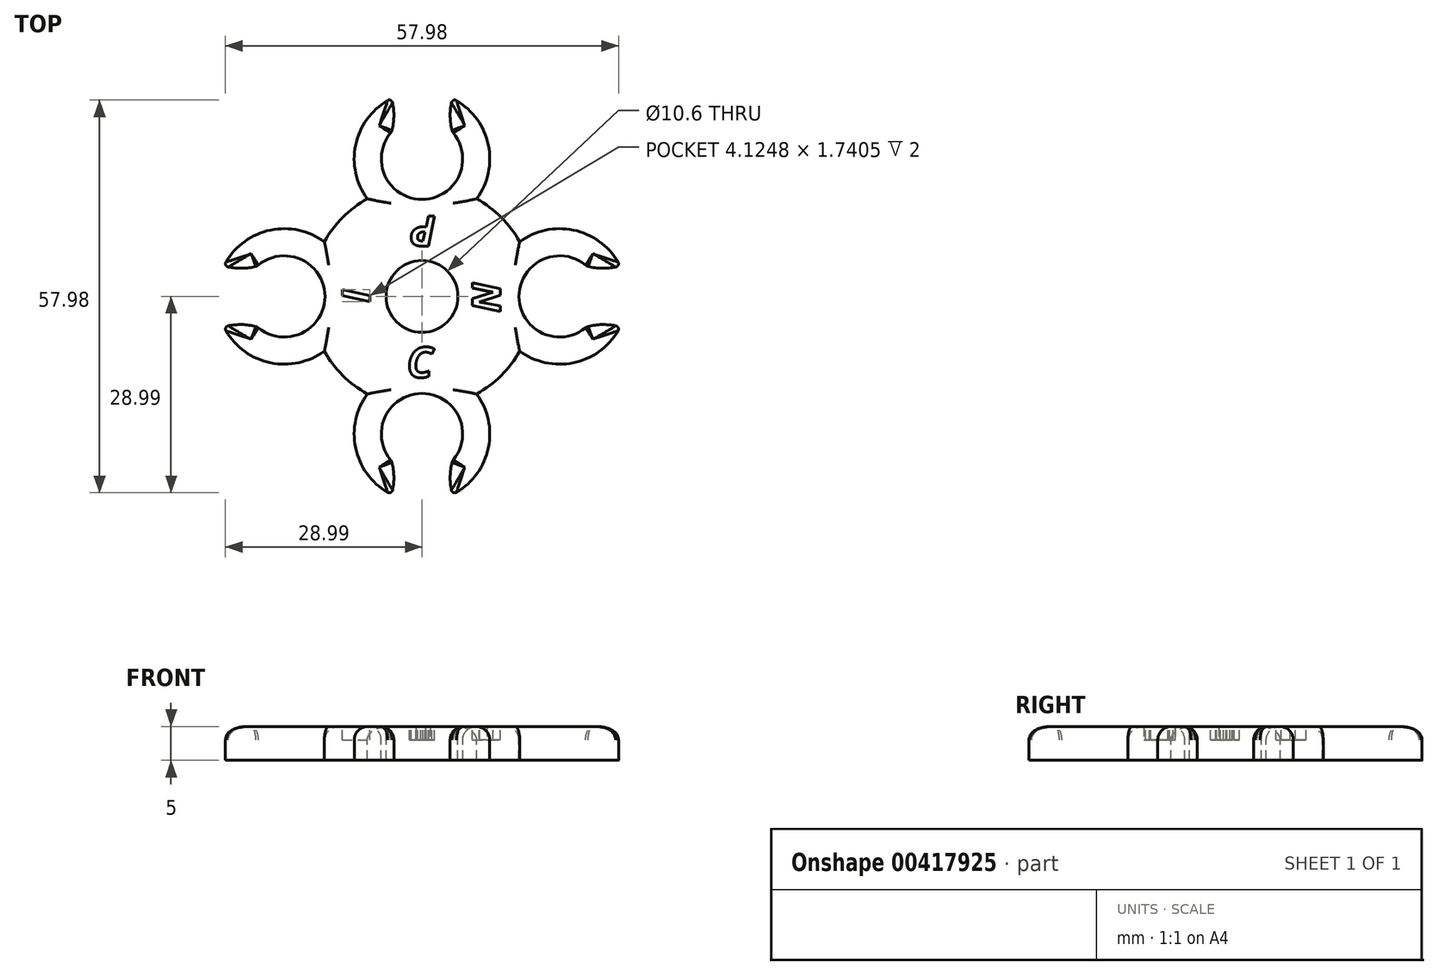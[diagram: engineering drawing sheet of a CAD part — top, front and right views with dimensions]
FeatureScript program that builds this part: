
annotation { "Feature Type Name" : "Feature", "Feature Type Description" : "" }
export const myFeature = defineFeature(function(context is Context, id is Id, definition is map)
    precondition{}
    {
        {
            var Q0;
            Q0=qCreatedBy(makeId("Top.planeOp"),FACE);
            var sketch = newSketch(context, id + "F0", { "sketchPlane" : qUnion([Q0])});
            skArc(sketch, "E0", {"start": v(24.12, 4.63) * mm, "mid": v(14.31, 0) * mm, "end": v(24.12, -4.63) * mm});
            skArc(sketch, "E1", {"start": v(28.92, 5.08) * mm, "mid": v(22.33, 9.8) * mm, "end": v(14.41, 8.07) * mm});
            skArc(sketch, "E2", {"start": v(24.5, 4.44) * mm, "mid": v(26.55, 4.15) * mm, "end": v(28.6, 4.34) * mm});
            skArc(sketch, "E3", {"start": v(28.6, -4.34) * mm, "mid": v(26.55, -4.15) * mm, "end": v(24.5, -4.44) * mm});
            skArc(sketch, "E4.filletArc", {"start": v(28.6, 4.34) * mm, "mid": v(28.95, 4.63) * mm, "end": v(28.92, 5.08) * mm});
            skArc(sketch, "E5.filletArc", {"start": v(28.92, -5.08) * mm, "mid": v(28.95, -4.63) * mm, "end": v(28.6, -4.34) * mm});
            skArc(sketch, "E6.filletArc", {"start": v(24.5, -4.44) * mm, "mid": v(24.3, -4.51) * mm, "end": v(24.12, -4.63) * mm});
            skArc(sketch, "E7.filletArc", {"start": v(24.12, 4.63) * mm, "mid": v(24.3, 4.51) * mm, "end": v(24.5, 4.44) * mm});
            skCircle(sketch, "E8", {"center": v(0, 0) * mm, "radius": 5.3 * mm});
            skArc(sketch, "E9.1.0", {"start": v(-4.63, 24.12) * mm, "mid": v(0, 14.31) * mm, "end": v(4.63, 24.12) * mm});
            skArc(sketch, "E9.1.1", {"start": v(-5.08, 28.92) * mm, "mid": v(-9.8, 22.33) * mm, "end": v(-8.07, 14.41) * mm});
            skArc(sketch, "E9.1.2", {"start": v(-4.44, 24.5) * mm, "mid": v(-4.15, 26.55) * mm, "end": v(-4.34, 28.6) * mm});
            skArc(sketch, "E9.1.3", {"start": v(4.34, 28.6) * mm, "mid": v(4.15, 26.55) * mm, "end": v(4.44, 24.5) * mm});
            skArc(sketch, "E9.1.4", {"start": v(4.44, 24.5) * mm, "mid": v(4.51, 24.3) * mm, "end": v(4.63, 24.12) * mm});
            skArc(sketch, "E9.1.5", {"start": v(-4.63, 24.12) * mm, "mid": v(-4.51, 24.3) * mm, "end": v(-4.44, 24.5) * mm});
            skArc(sketch, "E9.1.6", {"start": v(-4.34, 28.6) * mm, "mid": v(-4.63, 28.95) * mm, "end": v(-5.08, 28.92) * mm});
            skArc(sketch, "E9.1.7", {"start": v(5.08, 28.92) * mm, "mid": v(4.63, 28.95) * mm, "end": v(4.34, 28.6) * mm});
            skArc(sketch, "E9.2.0", {"start": v(-24.12, -4.63) * mm, "mid": v(-14.31, 0) * mm, "end": v(-24.12, 4.63) * mm});
            skArc(sketch, "E9.2.1", {"start": v(-28.92, -5.08) * mm, "mid": v(-22.33, -9.8) * mm, "end": v(-14.41, -8.07) * mm});
            skArc(sketch, "E9.2.2", {"start": v(-24.5, -4.44) * mm, "mid": v(-26.55, -4.15) * mm, "end": v(-28.6, -4.34) * mm});
            skArc(sketch, "E9.2.3", {"start": v(-28.6, 4.34) * mm, "mid": v(-26.55, 4.15) * mm, "end": v(-24.5, 4.44) * mm});
            skArc(sketch, "E9.2.4", {"start": v(-24.5, 4.44) * mm, "mid": v(-24.3, 4.51) * mm, "end": v(-24.12, 4.63) * mm});
            skArc(sketch, "E9.2.5", {"start": v(-24.12, -4.63) * mm, "mid": v(-24.3, -4.51) * mm, "end": v(-24.5, -4.44) * mm});
            skArc(sketch, "E9.2.6", {"start": v(-28.6, -4.34) * mm, "mid": v(-28.95, -4.63) * mm, "end": v(-28.92, -5.08) * mm});
            skArc(sketch, "E9.2.7", {"start": v(-28.92, 5.08) * mm, "mid": v(-28.95, 4.63) * mm, "end": v(-28.6, 4.34) * mm});
            skArc(sketch, "E9.3.0", {"start": v(4.63, -24.12) * mm, "mid": v(0, -14.31) * mm, "end": v(-4.63, -24.12) * mm});
            skArc(sketch, "E9.3.1", {"start": v(5.08, -28.92) * mm, "mid": v(9.8, -22.33) * mm, "end": v(8.07, -14.41) * mm});
            skArc(sketch, "E9.3.2", {"start": v(4.44, -24.5) * mm, "mid": v(4.15, -26.55) * mm, "end": v(4.34, -28.6) * mm});
            skArc(sketch, "E9.3.3", {"start": v(-4.34, -28.6) * mm, "mid": v(-4.15, -26.55) * mm, "end": v(-4.44, -24.5) * mm});
            skArc(sketch, "E9.3.4", {"start": v(-4.44, -24.5) * mm, "mid": v(-4.51, -24.3) * mm, "end": v(-4.63, -24.12) * mm});
            skArc(sketch, "E9.3.5", {"start": v(4.63, -24.12) * mm, "mid": v(4.51, -24.3) * mm, "end": v(4.44, -24.5) * mm});
            skArc(sketch, "E9.3.6", {"start": v(4.34, -28.6) * mm, "mid": v(4.63, -28.95) * mm, "end": v(5.08, -28.92) * mm});
            skArc(sketch, "E9.3.7", {"start": v(-5.08, -28.92) * mm, "mid": v(-4.63, -28.95) * mm, "end": v(-4.34, -28.6) * mm});
            skArc(sketch, "E10", {"start": v(-8.07, 14.41) * mm, "mid": v(-11.68, 11.68) * mm, "end": v(-14.41, 8.07) * mm});
            skArc(sketch, "E11.trimOffspring", {"start": v(14.41, 8.07) * mm, "mid": v(11.68, 11.68) * mm, "end": v(8.07, 14.41) * mm});
            skArc(sketch, "E12.trimOffspring", {"start": v(8.07, -14.41) * mm, "mid": v(11.68, -11.68) * mm, "end": v(14.41, -8.07) * mm});
            skArc(sketch, "E13.trimOffspring", {"start": v(-14.41, -8.07) * mm, "mid": v(-11.68, -11.68) * mm, "end": v(-8.07, -14.41) * mm});
            skLineSegment(sketch, "E14.bottom", {"start": v(-2.08, -7.47) * mm, "end": v(2.08, -7.47) * mm, "construction": true});
            skLineSegment(sketch, "E14.top", {"start": v(-2.08, -11.97) * mm, "end": v(2.08, -11.97) * mm, "construction": true});
            skLineSegment(sketch, "E14.left", {"start": v(-2.08, -7.47) * mm, "end": v(-2.08, -11.97) * mm, "construction": true});
            skLineSegment(sketch, "E14.right", {"start": v(2.08, -7.47) * mm, "end": v(2.08, -11.97) * mm, "construction": true});
            skPoint(sketch, "E14.middle", {"position": v(0, -9.72) * mm});
            skLineSegment(sketch, "E15.1.0", {"start": v(7.39, -2.08) * mm, "end": v(7.39, 2.08) * mm, "construction": true});
            skLineSegment(sketch, "E15.1.1", {"start": v(7.39, -2.08) * mm, "end": v(11.89, -2.08) * mm, "construction": true});
            skLineSegment(sketch, "E15.1.2", {"start": v(11.89, -2.08) * mm, "end": v(11.89, 2.08) * mm, "construction": true});
            skLineSegment(sketch, "E15.1.3", {"start": v(7.39, 2.08) * mm, "end": v(11.89, 2.08) * mm, "construction": true});
            skLineSegment(sketch, "E15.2.0", {"start": v(2, 7.39) * mm, "end": v(-2.16, 7.39) * mm, "construction": true});
            skLineSegment(sketch, "E15.2.1", {"start": v(2, 7.39) * mm, "end": v(2, 11.89) * mm, "construction": true});
            skLineSegment(sketch, "E15.2.2", {"start": v(2, 11.89) * mm, "end": v(-2.16, 11.89) * mm, "construction": true});
            skLineSegment(sketch, "E15.2.3", {"start": v(-2.16, 7.39) * mm, "end": v(-2.16, 11.89) * mm, "construction": true});
            skLineSegment(sketch, "E15.3.0", {"start": v(-7.47, 2) * mm, "end": v(-7.47, -2.16) * mm, "construction": true});
            skLineSegment(sketch, "E15.3.1", {"start": v(-7.47, 2) * mm, "end": v(-11.97, 2) * mm, "construction": true});
            skLineSegment(sketch, "E15.3.2", {"start": v(-11.97, 2) * mm, "end": v(-11.97, -2.16) * mm, "construction": true});
            skLineSegment(sketch, "E15.3.3", {"start": v(-7.47, -2.16) * mm, "end": v(-11.97, -2.16) * mm, "construction": true});
            skPoint(sketch, "E15.center", {"position": v(-0.04, -0.04) * mm});
            skText(sketch, "E16", { "text": "C", "fontName": "OpenSans-BoldItalic.ttf"});
            skText(sketch, "E17", { "text": "N", "fontName": "OpenSans-BoldItalic.ttf"});
            skText(sketch, "E18", { "text": "P", "fontName": "OpenSans-BoldItalic.ttf"});
            skText(sketch, "E19", { "text": "I", "fontName": "OpenSans-BoldItalic.ttf"});
            skArc(sketch, "E20.trimOffspring", {"start": v(-14.41, 8.07) * mm, "mid": v(-22.33, 9.8) * mm, "end": v(-28.92, 5.08) * mm});
            skArc(sketch, "E21.trimOffspring", {"start": v(-8.07, -14.41) * mm, "mid": v(-9.8, -22.33) * mm, "end": v(-5.08, -28.92) * mm});
            skArc(sketch, "E22.trimOffspring", {"start": v(14.41, -8.07) * mm, "mid": v(22.33, -9.8) * mm, "end": v(28.92, -5.08) * mm});
            skArc(sketch, "E23.trimOffspring", {"start": v(8.07, 14.41) * mm, "mid": v(9.8, 22.33) * mm, "end": v(5.08, 28.92) * mm});
            const initialGuessF0  = {"E16": [-0.00223, -0.01197, 1, 0, 0.0045], "E17": [0.01155, -0.00236, 0, 1, 0.00416], "E18": [0.00203, 0.01189, -1, 0, 0.0045], "E19": [-0.01178, 0.00113, 0, -1, 0.00416]};
            skSetInitialGuess(sketch, initialGuessF0);
            skSolve(sketch);
        }
        {
            var Q0;
            Q0=makeQuery(id+"F0.imprint","IMPRINT",FACE,{"disambiguationData":[TD([[makeQuery(id+"F0.imprint","IMPRINT",EDGE,{"derivedFrom":sQuery(id+"F0.wireOp",EDGE,"E19.sketch_text.stroke-0")}),-1.0]])]});
            var Q1;
            Q1=makeQuery(id+"F0.imprint","IMPRINT",FACE,{"disambiguationData":[TD([[makeQuery(id+"F0.imprint","IMPRINT",EDGE,{"derivedFrom":sQuery(id+"F0.wireOp",EDGE,"E8")}),-1.0]])]});
            var Q2;
            Q2=makeQuery(id+"F0.imprint","IMPRINT",FACE,{"disambiguationData":[TD([[makeQuery(id+"F0.imprint","IMPRINT",EDGE,{"derivedFrom":sQuery(id+"F0.wireOp",EDGE,"E18.sketch_text.stroke-0")}),-1.0]])]});
            var Q3;
            Q3=makeQuery(id+"F0.imprint","IMPRINT",FACE,{"disambiguationData":[TD([[makeQuery(id+"F0.imprint","IMPRINT",EDGE,{"derivedFrom":sQuery(id+"F0.wireOp",EDGE,"E18.sketch_text.stroke-0")}),1.0]])]});
            var Q4;
            Q4=makeQuery(id+"F0.imprint","IMPRINT",FACE,{"disambiguationData":[TD([[makeQuery(id+"F0.imprint","IMPRINT",EDGE,{"derivedFrom":sQuery(id+"F0.wireOp",EDGE,"E17.sketch_text.stroke-0")}),-1.0]])]});
            var Q5;
            Q5=makeQuery(id+"F0.imprint","IMPRINT",FACE,{"disambiguationData":[TD([[makeQuery(id+"F0.imprint","IMPRINT",EDGE,{"derivedFrom":sQuery(id+"F0.wireOp",EDGE,"E16.sketch_text.stroke-0")}),-1.0]])]});
            var Q6;
            Q6=makeQuery(id+"F0.imprint","IMPRINT",FACE,{"disambiguationData":[TD([[makeQuery(id+"F0.imprint","IMPRINT",EDGE,{"derivedFrom":sQuery(id+"F0.wireOp",EDGE,"E0")}),-1.0]])]});
            var Q7;
            Q7=makeQuery(id+"F0.imprint","IMPRINT",FACE,{"disambiguationData":[TD([[makeQuery(id+"F0.imprint","IMPRINT",EDGE,{"derivedFrom":sQuery(id+"F0.wireOp",EDGE,"E9.3.0")}),-1.0]])]});
            var Q8;
            Q8=makeQuery(id+"F0.imprint","IMPRINT",FACE,{"disambiguationData":[TD([[makeQuery(id+"F0.imprint","IMPRINT",EDGE,{"derivedFrom":sQuery(id+"F0.wireOp",EDGE,"E9.2.0")}),-1.0]])]});
            var Q9;
            Q9=makeQuery(id+"F0.imprint","IMPRINT",FACE,{"disambiguationData":[TD([[makeQuery(id+"F0.imprint","IMPRINT",EDGE,{"derivedFrom":sQuery(id+"F0.wireOp",EDGE,"E9.1.0")}),-1.0]])]});
            extrude(context, id + "F1", {"entities" : qUnion([Q0, Q1, Q2, Q3, Q4, Q5, Q6, Q7, Q8, Q9]), "oppositeDirection" : true, "depth" : 5 * mm, "offsetDistance" : 25 * mm});
        }
        {
            var Q0;
            Q0=makeQuery(id+"F0.imprint","IMPRINT",FACE,{"disambiguationData":[TD([[makeQuery(id+"F0.imprint","IMPRINT",EDGE,{"derivedFrom":sQuery(id+"F0.wireOp",EDGE,"E19.sketch_text.stroke-0")}),-1.0]])]});
            var Q1;
            Q1=makeQuery(id+"F0.imprint","IMPRINT",FACE,{"disambiguationData":[TD([[makeQuery(id+"F0.imprint","IMPRINT",EDGE,{"derivedFrom":sQuery(id+"F0.wireOp",EDGE,"E18.sketch_text.stroke-0")}),-1.0]])]});
            var Q2;
            Q2=makeQuery(id+"F0.imprint","IMPRINT",FACE,{"disambiguationData":[TD([[makeQuery(id+"F0.imprint","IMPRINT",EDGE,{"derivedFrom":sQuery(id+"F0.wireOp",EDGE,"E17.sketch_text.stroke-0")}),-1.0]])]});
            var Q3;
            Q3=makeQuery(id+"F0.imprint","IMPRINT",FACE,{"disambiguationData":[TD([[makeQuery(id+"F0.imprint","IMPRINT",EDGE,{"derivedFrom":sQuery(id+"F0.wireOp",EDGE,"E16.sketch_text.stroke-0")}),-1.0]])]});
            extrude(context, id + "F2", {"entities" : qUnion([Q0, Q1, Q2, Q3]), "operationType" : NewBodyOperationType.REMOVE, "oppositeDirection" : true, "depth" : 2 * mm, "offsetDistance" : 25 * mm});
        }
        {
            var Q0;
            {var subQ0=sQuery(id+"F0.wireOp",EDGE,"E9.1.1");Q0=makeQuery(id+"F1.opExtrude","CAP_EDGE",EDGE,{"disambiguationData":[OSD([subQ0]),TDD([makeQuery(id+"F0.imprint","IMPRINT",EDGE,{"disambiguationData":[TD([[makeQuery(id+"F0.imprint","INTERSECT",VERTEX,{"derivedFrom":[subQ0,sQuery(id+"F0.wireOp",EDGE,"E9.1.6")]}),-1.0]])],"derivedFrom":subQ0})])],"isStart":true});}
            var Q1;
            {var subQ0=sQuery(id+"F0.wireOp",EDGE,"E9.2.1");Q1=makeQuery(id+"F1.opExtrude","CAP_EDGE",EDGE,{"disambiguationData":[OSD([subQ0]),TDD([makeQuery(id+"F0.imprint","IMPRINT",EDGE,{"disambiguationData":[TD([[makeQuery(id+"F0.imprint","INTERSECT",VERTEX,{"derivedFrom":[subQ0,sQuery(id+"F0.wireOp",EDGE,"E9.2.7")]}),1.0]])],"derivedFrom":subQ0})])],"isStart":true});}
            var Q2;
            {var subQ0=sQuery(id+"F0.wireOp",EDGE,"E1");Q2=makeQuery(id+"F1.opExtrude","CAP_EDGE",EDGE,{"disambiguationData":[OSD([subQ0]),TDD([makeQuery(id+"F0.imprint","IMPRINT",EDGE,{"disambiguationData":[TD([[makeQuery(id+"F0.imprint","INTERSECT",VERTEX,{"derivedFrom":[subQ0,sQuery(id+"F0.wireOp",EDGE,"E4.filletArc")]}),-1.0]])],"derivedFrom":subQ0})])],"isStart":true});}
            var Q3;
            Q3=makeQuery(id+"F1.opExtrude","CAP_EDGE",EDGE,{"disambiguationData":[OSD([sQuery(id+"F0.wireOp",EDGE,"E10")])],"isStart":true});
            var Q4;
            {var subQ0=sQuery(id+"F0.wireOp",EDGE,"E9.3.1");Q4=makeQuery(id+"F1.opExtrude","CAP_EDGE",EDGE,{"disambiguationData":[OSD([subQ0]),TDD([makeQuery(id+"F0.imprint","IMPRINT",EDGE,{"disambiguationData":[TD([[makeQuery(id+"F0.imprint","INTERSECT",VERTEX,{"derivedFrom":[subQ0,sQuery(id+"F0.wireOp",EDGE,"E9.3.7")]}),1.0]])],"derivedFrom":subQ0})])],"isStart":true});}
            var Q5;
            Q5=makeQuery(id+"F1.opExtrude","CAP_EDGE",EDGE,{"disambiguationData":[OSD([sQuery(id+"F0.wireOp",EDGE,"E13.trimOffspring")])],"isStart":true});
            var Q6;
            Q6=makeQuery(id+"F1.opExtrude","CAP_EDGE",EDGE,{"disambiguationData":[OSD([sQuery(id+"F0.wireOp",EDGE,"E12.trimOffspring")])],"isStart":true});
            var Q7;
            Q7=makeQuery(id+"F1.opExtrude","CAP_EDGE",EDGE,{"disambiguationData":[OSD([sQuery(id+"F0.wireOp",EDGE,"E11.trimOffspring")])],"isStart":true});
            fillet(context, id + "F3", {"entities" : qUnion([Q0, Q1, Q2, Q3, Q4, Q5, Q6, Q7]), "radius" : 2 * mm, "tangentPropagation" : true, "allowEdgeOverflow" : false});
        }
    });
